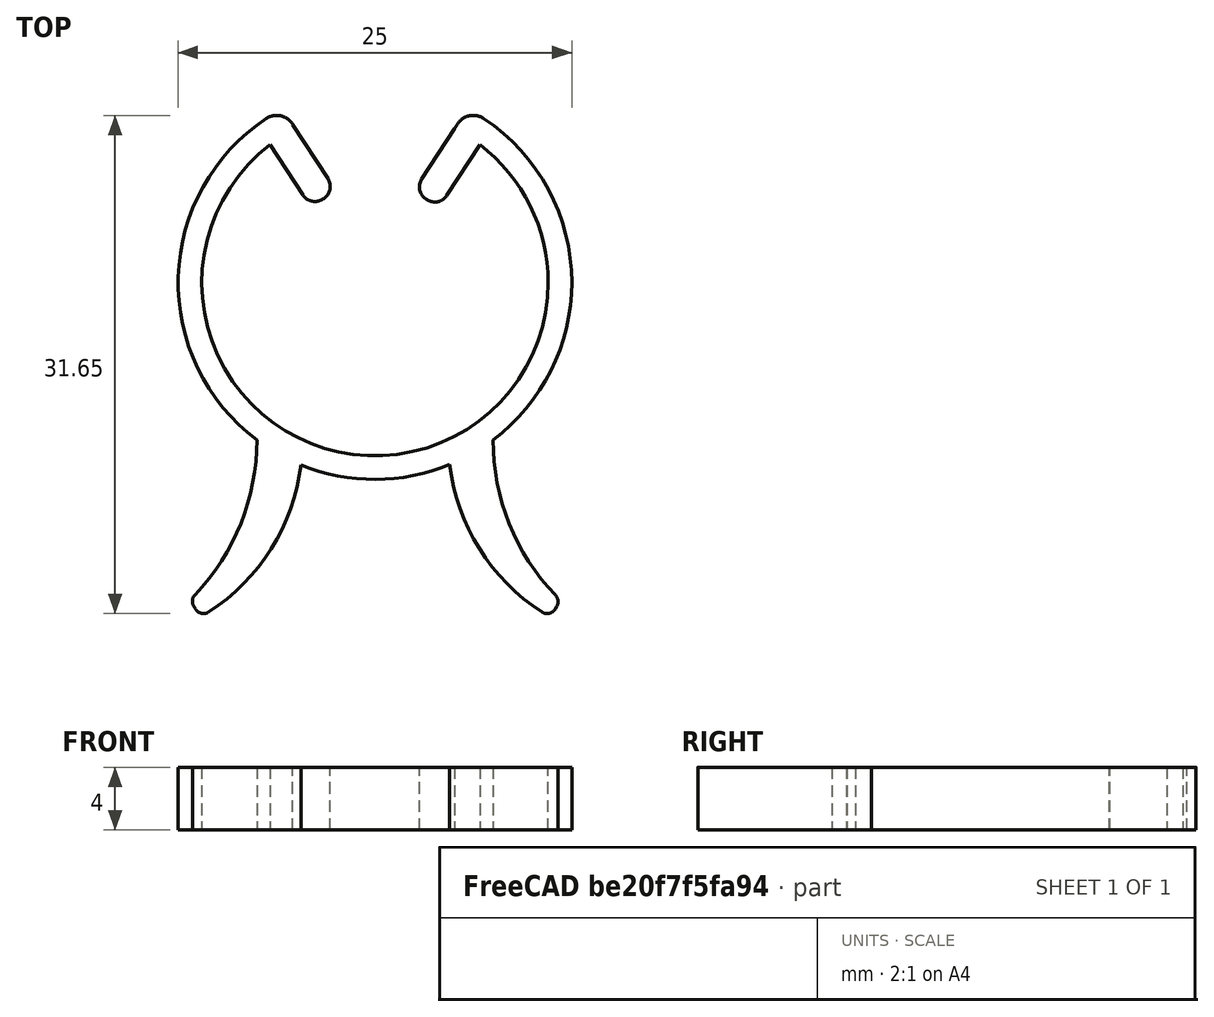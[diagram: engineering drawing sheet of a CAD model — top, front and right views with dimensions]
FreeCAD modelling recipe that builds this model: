
FCSTD DOCUMENT  (FreeCAD 0.21RUnknown)
Label: plant clip
License: All rights reserved
LicenseURL: https://en.wikipedia.org/wiki/All_rights_reserved
objects: PartDesign::SubtractiveCylinder×4, PartDesign::AdditiveCylinder×3, PartDesign::Fillet×3, PartDesign::AdditiveBox×2, PartDesign::Body×1
note: 25 computed .brp shape members not serialized (recipe doc carries the construction recipe); baked Part::Feature solids carry a one-line shape summary decoded from their .brp

FEATURE [PartDesign::AdditiveCylinder] Cylinder
  Angle = 360
  AttacherType = Attacher::AttachEngine3D
  FirstAngle = 0
  Height = 4
  MapMode = 5
  Radius = 12.5
  SecondAngle = 0
  Support = -> [XY_Plane]
FEATURE [PartDesign::SubtractiveCylinder] Cylinder001
  Angle = 360
  AttacherType = Attacher::AttachEngine3D
  BaseFeature = -> Cylinder
  FirstAngle = 0
  Height = 4
  Radius = 11
  SecondAngle = 0
FEATURE [PartDesign::SubtractiveCylinder] Cylinder002
  Angle = 66
  AttacherType = Attacher::AttachEngine3D
  AttachmentOffset = pos=(0,2,0) rot=(0,0,1;0.994838rad)
  BaseFeature = -> Cylinder001
  FirstAngle = 0
  Height = 4
  MapMode = 5
  Placement = pos=(0,2,0) rot=(0,0,1;0.994838rad)
  Radius = 11
  SecondAngle = 0
  Support = -> [XY_Plane]
FEATURE [PartDesign::AdditiveBox] Box
  AttacherType = Attacher::AttachEngine3D
  AttachmentOffset = pos=(5.2,10,0) rot=(0,0,1;4.13643rad)
  BaseFeature = -> Cylinder002
  Height = 4
  Length = 5
  MapMode = 5
  Placement = pos=(5.2,10,0) rot=(0,0,1;4.13643rad)
  Support = -> [XY_Plane]
  Width = 1.9
FEATURE [PartDesign::AdditiveBox] Box001
  AttacherType = Attacher::AttachEngine3D
  AttachmentOffset = pos=(-6.811,9,0) rot=(0,0,-1;0.994838rad)
  BaseFeature = -> Box
  Height = 4
  Length = 5
  MapMode = 5
  Placement = pos=(-6.811,9,0) rot=(0,0,-1;0.994838rad)
  Support = -> [XY_Plane]
  Width = 1.9
FEATURE [PartDesign::AdditiveCylinder] Cylinder003
  Angle = 60
  AttacherType = Attacher::AttachEngine3D
  AttachmentOffset = pos=(17.65,-10,0) rot=(0,0,1;3.14159rad)
  BaseFeature = -> Box001
  FirstAngle = 0
  Height = 4
  MapMode = 5
  Placement = pos=(17.65,-10,0) rot=(0,0,1;3.14159rad)
  Radius = 13
  SecondAngle = 0
  Support = -> [XY_Plane]
FEATURE [PartDesign::SubtractiveCylinder] Cylinder004
  Angle = 46
  AttacherType = Attacher::AttachEngine3D
  AttachmentOffset = pos=(21.75,-10,0) rot=(0,0,1;3.14159rad)
  BaseFeature = -> Cylinder003
  FirstAngle = 0
  Height = 4
  MapMode = 5
  Placement = pos=(21.75,-10,0) rot=(0,0,1;3.14159rad)
  Radius = 14.25
  SecondAngle = 0
  Support = -> [XY_Plane]
FEATURE [PartDesign::AdditiveCylinder] Cylinder005
  Angle = 60
  AttacherType = Attacher::AttachEngine3D
  AttachmentOffset = pos=(-17.6,-10,0) rot=(0,0,-1;1.0472rad)
  BaseFeature = -> Cylinder004
  FirstAngle = 0
  Height = 4
  MapMode = 5
  Placement = pos=(-17.6,-10,0) rot=(0,0,-1;1.0472rad)
  Radius = 13
  SecondAngle = 0
  Support = -> [XY_Plane]
FEATURE [PartDesign::SubtractiveCylinder] Cylinder006
  Angle = 46
  AttacherType = Attacher::AttachEngine3D
  AttachmentOffset = pos=(-21.75,-10,0) rot=(0,0,-1;0.802851rad)
  BaseFeature = -> Cylinder005
  FirstAngle = 0
  Height = 4
  MapMode = 5
  Placement = pos=(-21.75,-10,0) rot=(0,0,-1;0.802851rad)
  Radius = 14.25
  SecondAngle = 0
  Support = -> [XY_Plane]
FEATURE [PartDesign::Fillet] Fillet
  Base = -> Cylinder006 [Edge67,Edge94,Edge70,Edge74]
  BaseFeature = -> Cylinder006
  Placement = pos=(-21.75,-10,0) rot=(0,0,-1;0.802851rad)
  Radius = 0.9
  SupportTransform = false
  UseAllEdges = false
FEATURE [PartDesign::Fillet] Fillet001
  Base = -> Fillet [Edge97,Edge89,Edge75,Edge95]
  BaseFeature = -> Fillet
  Placement = pos=(-21.75,-10,0) rot=(0,0,-1;0.802851rad)
  Radius = 0.6
  SupportTransform = false
  UseAllEdges = false
FEATURE [PartDesign::Fillet] Fillet002
  Base = -> Fillet001 [Edge13,Edge66]
  BaseFeature = -> Fillet001
  Placement = pos=(-21.75,-10,0) rot=(0,0,-1;0.802851rad)
  Radius = 1.2
  SupportTransform = false
  UseAllEdges = false
FEATURE [PartDesign::Body] Body  label="plant clip"
  Group = -> [Cylinder,Cylinder001,Cylinder002,Box,Box001,Cylinder003,Cylinder004,Cylinder005,Cylinder006,Fillet,Fillet001,Fillet002]
  Origin = -> Origin
  Tip = -> Fillet002
